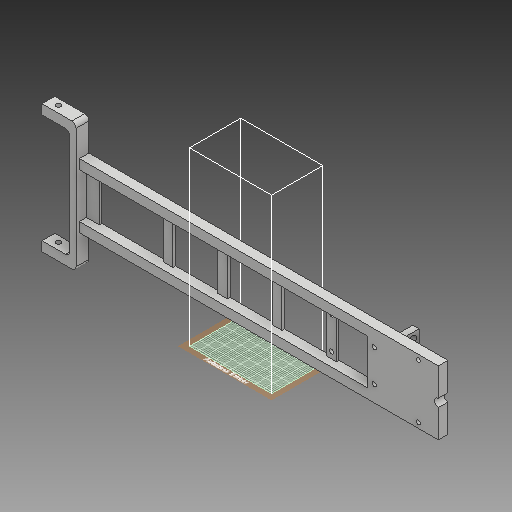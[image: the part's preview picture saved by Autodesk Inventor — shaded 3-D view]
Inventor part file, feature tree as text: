
AUTODESK INVENTOR PART (.ipt)
format: ipt  version: 2018 (Build 220112000, 112)  size: 857,088 bytes
history: native  units: mm
features: sketch x52, extrude x40, fillet x13, hole x6, plane x1
ambient origin geometry x8: Origin, YZ Plane, XZ Plane, XY Plane, X Axis, Y Axis, Z Axis, Center Point
bodies: Solid1 (feature_tree)
feature tree (112):
  extrude  "Extrusion1"  Depth=50.0mm
  hole  "Hole1"  [1 undecoded]
  hole  "Hole2"  [1 undecoded]
  extrude  "Extrusion2"  Depth=25.0mm
  extrude  "Extrusion3"  Depth=25.0mm
  extrude  "Extrusion4"  Depth=5.0mm
  sketch  "Sketch7"  dims[d25=10.0mm d26=5.0mm]
  extrude  "Extrusion5"  Depth=5.0mm
  extrude  "Extrusion6"  Depth=35.0mm
  extrude  "Extrusion7"  Depth=35.0mm
  extrude  "Extrusion8"  Depth=35.0mm
  extrude  "Extrusion9"  Depth=2.0mm TaperAngle=0.0deg
  extrude  "Extrusion10"  Depth=7.5mm TaperAngle=0.0deg
  extrude  "Extrusion11"  Depth=10.0mm
  extrude  "Extrusion12"  Depth=7.5mm
  fillet  "Fillet1"  Radius=7.5mm
  fillet  "Fillet2"  Radius=25.0mm
  fillet  "Fillet3"  Radius=3.0mm
  fillet  "Fillet4"  Radius=3.2mm
  fillet  "Fillet5"  Radius=2.1mm
  fillet  "Fillet6"  Radius=5.5mm
  extrude  "Extrusion13"  Depth=92.5mm TaperAngle=0.0deg
  sketch  "Sketch17"  dims[d58=4.25mm d59=241.0mm d60=0.0mm]
  hole  "Hole3"  [1 undecoded]
  hole  "Hole4"  [1 undecoded]
  extrude  "Extrusion14"  Depth=5.0mm
  extrude  "Extrusion15"  Depth=2.5mm TaperAngle=0.0deg
  extrude  "Extrusion16"  Depth=6.35mm
  extrude  "Extrusion17"  Depth=2.5mm
  extrude  "Extrusion18"  Depth=14.55mm TaperAngle=0.0deg
  extrude  "Extrusion19"  Depth=0.1mm
  extrude  "Extrusion20"  Depth=3.25mm
  extrude  "Extrusion21"  Depth=3.25mm
  hole  "Hole5"  [1 undecoded]
  extrude  "Extrusion22"  Depth=2.0mm
  extrude  "Extrusion23"  Depth=15.0mm
  extrude  "Extrusion24"  Depth=10.0mm TaperAngle=0.0deg
  hole  "Hole6"  [1 undecoded]
  extrude  "Extrusion25"  Depth=100.0mm TaperAngle=0.0deg
  extrude  "Extrusion26"  Depth=2.0mm TaperAngle=0.0deg
  sketch  "Sketch35"  dims[d116=3.3mm d117=3.3mm]
  plane  "Work Plane1"
  sketch  "Sketch36"  dims[d118=3.3mm d119=3.3mm d120=2.0mm d121=0.0mm]
  extrude  "Extrusion27"  Depth=3.3mm
  extrude  "Extrusion28"  Depth=2.0mm
  fillet  "Fillet7"  Radius=2.0mm
  extrude  "Extrusion29"  Depth=8.0mm
  extrude  "Extrusion30"  Depth=21.0mm
  extrude  "Extrusion31"  Depth=8.5mm
  extrude  "Extrusion32"  Depth=3.5mm
  sketch  "Sketch43"  dims[d142=10.0mm d143=0.0mm d144=7.5mm d145=0.0mm]
  fillet  "Fillet8"  Radius=3.3mm
  extrude  "Extrusion33"  Depth=3.3mm
  extrude  "Extrusion34"  Depth=7.5mm TaperAngle=0.0deg
  extrude  "Extrusion35"  Depth=15.0mm
  extrude  "Extrusion36"  Depth=100.0mm TaperAngle=0.0deg
  extrude  "Extrusion37"  Depth=5.0mm
  fillet  "Fillet9"  Radius=5.0mm
  fillet  "Fillet10"  Radius=37.5mm
  fillet  "Fillet11"  Radius=1.1mm
  fillet  "Fillet12"  Radius=37.5mm
  sketch  "Sketch49"  dims[d170=5.5mm d171=0.0mm d172=10.0mm d173=0.0mm]
  extrude  "Extrusion38"  Depth=0.2mm
  extrude  "Extrusion39"  Depth=10.0mm TaperAngle=0.0deg
  extrude  "Extrusion40"  Depth=74.724mm
  fillet  "Fillet13"  Radius=85.515mm
  sketch  "Sketch1"  dims[d0=50.0mm d1=50.0mm]
  sketch  "Sketch2"  dims[d2=240.0mm d3=7.5mm]
  sketch  "Sketch3"  dims[d4=7.5mm d5=7.5mm d6=0.0mm]
  sketch  "Sketch4"  dims[d7=6.35mm d8=6.0mm d9=4.0mm d10=2.0mm d11=90.0deg d12=8.0mm d13=20.594885mm d14=25.0mm]
  sketch  "Sketch5"  dims[d15=3.3mm d16=6.0mm d17=4.0mm d18=2.0mm d19=90.0deg d20=8.0mm d21=20.594885mm d22=25.0mm]
  sketch  "Sketch6"  dims[d23=180.0deg d24=5.0mm]
  sketch  "Sketch8"  dims[d27=17.5mm d28=0.0mm d30=35.0mm]
  sketch  "Sketch9"  dims[d31=35.0mm d32=35.0mm]
  sketch  "Sketch10"  dims[d33=35.0mm d34=35.0mm]
  sketch  "Sketch11"  dims[d35=35.0mm d36=2.0mm d37=0.0mm]
  sketch  "Sketch12"  dims[d38=10.0mm d39=7.5mm d40=0.0mm]
  sketch  "Sketch13"  dims[d41=100.0mm d42=10.0mm]
  sketch  "Sketch14"  dims[d43=7.5mm d44=0.0mm d45=7.5mm d46=7.5mm d47=25.0mm d48=0.0mm d49=3.0mm d50=3.2mm d51=2.1mm d52=5.5mm]
  sketch  "Sketch15"  dims[d53=3.3mm d54=92.5mm d55=0.0mm]
  sketch  "Sketch16"  dims[d56=5.5mm d57=3.3mm]
  sketch  "Sketch18"  dims[d61=4.44mm d62=5.0mm]
  sketch  "Sketch19"  dims[d63=2.5mm d64=91.25mm d65=0.0mm]
  sketch  "Sketch20"  dims[d66=30.0mm d67=6.35mm]
  sketch  "Sketch21"  dims[d68=3.8mm d69=0.0mm d70=2.5mm]
  sketch  "Sketch22"  dims[d71=14.55mm d72=0.0mm d73=14.55mm d74=0.0mm]
  sketch  "Sketch23"  dims[d75=0.1mm d76=0.1mm]
  sketch  "Sketch24"  dims[d77=3.25mm d78=3.25mm]
  sketch  "Sketch25"  dims[d79=3.25mm d80=3.25mm]
  sketch  "Sketch26"  dims[d81=35.0mm d82=10.0mm]
  sketch  "Sketch27"  dims[d83=2.0mm d84=0.0mm d85=3.6mm]
  sketch  "Sketch28"  dims[d86=3.6mm]
  sketch  "Sketch29"  dims[d87=3.3mm d88=6.0mm d89=4.0mm d90=2.0mm d91=90.0deg d92=15.0mm d93=20.594885mm]
  sketch  "Sketch30"  dims[d94=3.3mm d95=6.0mm d96=4.0mm d97=2.0mm d98=90.0deg d99=15.0mm d100=20.594885mm d101=6.0mm]
  sketch  "Sketch31"  dims[d102=20.0mm d103=0.0mm d104=10.0mm d105=0.0mm]
  sketch  "Sketch32"  dims[d106=2.0mm d107=0.0mm d108=4.0mm]
  sketch  "Sketch33"  dims[d109=100.0mm d110=0.0mm d111=100.0mm d112=0.0mm]
  sketch  "Sketch34"  dims[d113=5.0mm d114=2.0mm d115=0.0mm]
  sketch  "Sketch37"  dims[d122=5.5mm d123=0.0mm]
  sketch  "Sketch38"  dims[d124=3.3mm d125=6.0mm d126=4.0mm d127=2.0mm d128=90.0deg d129=8.0mm d130=20.594885mm d131=42.0mm]
  sketch  "Sketch39"  dims[d132=17.0mm d133=21.0mm]
  sketch  "Sketch40"  dims[d135=8.5mm d136=15.825mm]
  sketch  "Sketch41"  dims[d137=3.5mm d138=21.0mm d139=3.3mm]
  sketch  "Sketch42"  dims[d140=3.3mm d141=3.3mm]
  sketch  "Sketch44"  dims[d146=100.0mm d147=0.0mm]
  sketch  "Sketch45"  dims[d148=5.0mm d149=6.0mm d150=4.0mm d151=2.0mm d152=90.0deg d153=15.0mm d154=0.0mm d155=3.75mm]
  sketch  "Sketch46"  dims[d156=100.0mm d157=0.0mm d158=100.0mm d159=0.0mm]
  sketch  "Sketch47"  dims[d160=-0.698132mm d161=5.0mm d162=5.0mm d163=37.5mm d164=0.0mm d165=1.1mm d166=37.5mm d167=0.0mm]
  sketch  "Sketch48"  dims[d168=0.2mm d169=3.0mm]
  sketch  "Sketch50"  dims[d174=74.724mm d175=74.724mm d176=85.515mm]
  sketch  "Sketch51"  dims[d177=5.0mm]
  sketch  "Sketch52"  dims[d178=85.515mm d179=5.0mm d180=85.515mm d181=5.0mm d182=85.515mm d183=5.0mm d184=2.0mm d185=0.0mm d186=10.0mm d187=2.0mm d188=0.0mm d189=2.0mm d190=1.0mm d191=0.0mm d192=2.0mm d193=0.0mm d194=10.0mm d195=1.0mm d196=0.0mm d197=20.0mm d198=1.0mm d199=0.0mm d200=7.5mm d201=5.0mm d202=2.5mm d203=0.0mm d204=3.25mm d205=3.25mm d206=3.25mm d207=3.25mm d208=6.25mm d209=9.58mm d210=250.0mm d211=0.0mm d212=5.25mm d213=4.3mm d214=0.0mm d215=4.3mm d216=0.0mm d217=3.25mm]
note: 6 required parameter values undecoded (feature->parameter linkage not recoverable at this tier; creation-order binding heuristic only, values carry confidence <= 0.55)
